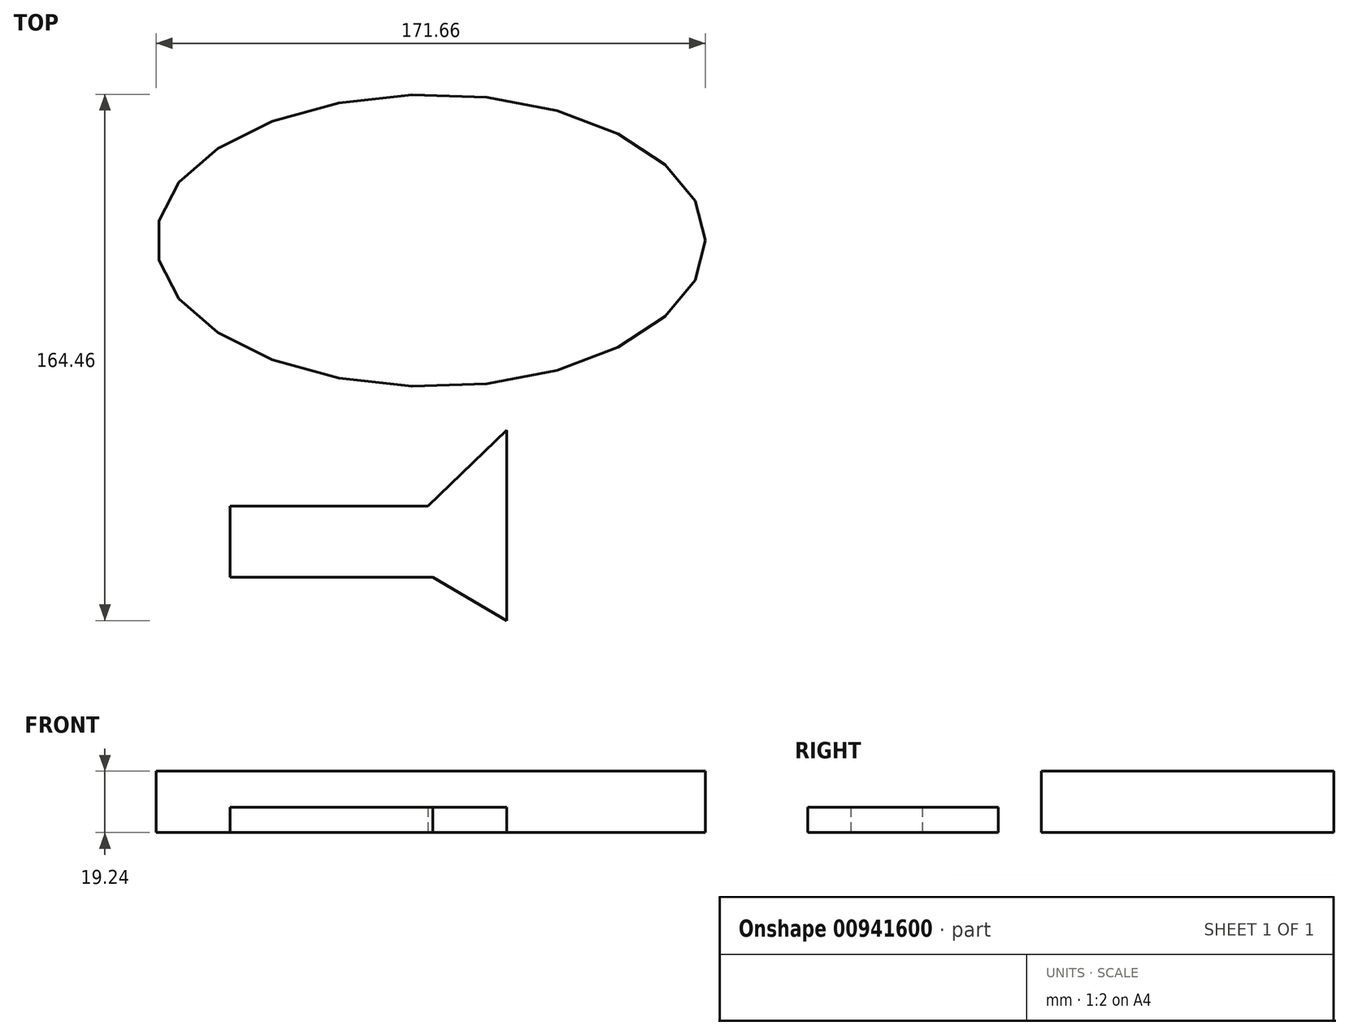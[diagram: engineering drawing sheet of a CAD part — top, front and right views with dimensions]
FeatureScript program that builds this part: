
annotation { "Feature Type Name" : "Feature", "Feature Type Description" : "" }
export const myFeature = defineFeature(function(context is Context, id is Id, definition is map)
    precondition{}
    {
        {
            var Q0;
            Q0=qCreatedBy(makeId("Top.planeOp"),FACE);
            var sketch = newSketch(context, id + "F0", { "sketchPlane" : qUnion([Q0])});
            skEllipse(sketch, "E0", {"center": v(-41.65, 18.4) * mm, "majorRadius": 85.83 * mm, "minorRadius": 45.67 * mm, "majorAxis": v(1, 0)});
            skSolve(sketch);
        }
        {
            var Q0;
            Q0 = qSketchRegion(id + "F0", true);
            extrude(context, id + "F1", {"entities" : qUnion([Q0]), "depth" : 19.24 * mm, "offsetDistance" : 25.4 * mm});
        }
        {
            var Q0;
            Q0=qCreatedBy(makeId("Top.planeOp"),FACE);
            var sketch = newSketch(context, id + "F2", { "sketchPlane" : qUnion([Q0])});
            skLineSegment(sketch, "E1", {"start": v(-104.45, -64.54) * mm, "end": v(-42.6, -64.54) * mm});
            skLineSegment(sketch, "E2", {"start": v(-42.6, -64.54) * mm, "end": v(-17.9, -40.8) * mm});
            skLineSegment(sketch, "E3", {"start": v(-17.9, -40.8) * mm, "end": v(-17.9, -100.4) * mm});
            skLineSegment(sketch, "E4", {"start": v(-17.9, -100.4) * mm, "end": v(-40.96, -86.88) * mm});
            skLineSegment(sketch, "E5", {"start": v(-40.96, -86.88) * mm, "end": v(-104.45, -86.88) * mm});
            skLineSegment(sketch, "E6", {"start": v(-104.45, -86.88) * mm, "end": v(-104.45, -64.54) * mm});
            skSolve(sketch);
        }
        {
            var Q0;
            Q0 = qSketchRegion(id + "F2", true);
            extrude(context, id + "F3", {"entities" : qUnion([Q0]), "depth" : 7.88 * mm, "offsetDistance" : 25.4 * mm});
        }
    });
